# Revit family: OKA-W, Kanaleinheit, blind, rastend, Höhe 60-110mm
name_source: partatom
category: Generic Models
revit_build: Autodesk Revit 2015 (Build: 20140606_1530(x64)
units: mm (PartAtom-declared; Revit-internal decimal feet)

## types (5) — shared parameters
Manufacturer = OBO Bettermann
Material = Steel, Galvanized
URL = http://www.obo-bettermann.com

## per-type parameters (varying)
| type | GTIN | Manufacturer Art. No. | Width |
| OKA-W2006050R | 4012195244424

4012195244424
4012195244424 | 7424480 | 200 mm  [stored 0.656168 ft] |
| OKA-W3006050R | 4012195244431

4012195244431

4012195244431

4012195244431

4012195244431
4012195244431 | 7424482 | 300 mm  [stored 0.984252 ft] |
| OKA-W4006050R | 4012195244448

4012195244448

2.4
4012195244448 | 7424484 | 400 mm  [stored 1.31234 ft] |
| OKA-W5006050R | 4012195244455 | 7424486

7424486 | 500 mm  [stored 1.64042 ft] |
| OKA-W6006050R | 4012195244462 | 7424488 | 600 mm |

note: column(s) folded — value = type name in every type: Article Type

note: [stored X ft] marks values corroborated as IEEE doubles in the binary element streams (Revit-internal decimal feet)

## geometry (parser evidence)
native form markers: Sweep x2
no freeform markers — native parametric forms only
